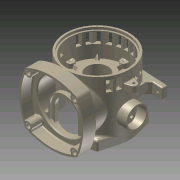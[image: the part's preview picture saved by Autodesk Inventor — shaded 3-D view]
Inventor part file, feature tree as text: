
AUTODESK INVENTOR PART (.ipt)
format: ipt  version: 2011 (Build 150239000, 239)  size: 2,364,928 bytes
history: native  units: in
note: dims shown in document units (in); Inventor stores cm internally (conversion verified against a paired STEP export)
features: extrude x28, sketch x24, plane x15, projected_geometry x10, loft x4, fillet x3, mirror x1, revolve x1, pattern_circular x1, chamfer x1
ambient origin geometry x8: Origin, YZ Plane, XZ Plane, XY Plane, X Axis, Y Axis, Z Axis, Center Point
bodies: Solid1 (feature_tree)
feature tree (88):
  extrude  "Extrusion1"  Depth=2.425in
  extrude  "Extrusion2"  Depth=0.1625in
  plane  "Work Plane3"
  sketch  "Sketch4"  dims[d7=3.375in d8=0.1in]
  plane  "Work Plane4"
  extrude  "Extrusion3"  Depth=0.1in
  sketch  "Sketch6"  dims[d11=0.1in d15=2.6693in]
  extrude  "Extrusion6"  Depth=0.1in
  extrude  "Extrusion7"  Depth=2.6693in
  sketch  "Sketch8"  dims[d19=2.625in d20=0.1in d21=0.0in]
  extrude  "Extrusion8"  Depth=0.575in TaperAngle=0.0deg
  extrude  "Extrusion10"  Depth=0.1in TaperAngle=0.0deg
  plane  "Work Plane5"
  sketch  "Sketch9"  dims[d24=3.15in d25=0.1in]
  extrude  "Extrusion12"  Depth=0.1in
  extrude  "Extrusion13"  Depth=0.1625in
  plane  "Work Plane6"
  extrude  "Extrusion15"  Depth=0.1in TaperAngle=0.0deg
  extrude  "Extrusion16"  Depth=0.5in TaperAngle=0.0deg
  plane  "Work Plane7"
  plane  "Work Plane8"
  plane  "Work Plane9"
  sketch  "Sketch15"  dims[d43=2.725in d44=0.0in d47=2.725in d48=0.0in]
  sketch  "Sketch13"  dims[d35=0.1in d38=0.5in d39=0.0in]
  extrude  "Extrusion19"  Depth=0.1in
  extrude  "Extrusion20"  Depth=2.725in TaperAngle=0.0deg
  plane  "Work Plane11"
  sketch  "Sketch14"  dims[d40=2.725in d41=0.0in d42=0.1in]
  extrude  "Extrusion21"  Depth=1.7in
  plane  "Work Plane12"
  extrude  "Extrusion22"  Depth=0.25in
  mirror  "Mirror3"
  extrude  "Extrusion23"  Depth=2.725in TaperAngle=0.0deg
  plane  "Work Plane15"
  sketch  "Sketch20"  dims[d55=0.0625in d58=2.725in d59=0.0in]
  plane  "Work Plane16"
  plane  "Work Plane17"
  extrude  "Extrusion30"  Depth=0.1in TaperAngle=0.0deg
  extrude  "Extrusion25"  Depth=0.75in
  extrude  "Extrusion26"  Depth=1.185in
  extrude  "Extrusion27"  Depth=0.25in TaperAngle=0.0deg
  extrude  "Extrusion29"  TaperAngle=0.0deg  [1 undecoded]
  extrude  "Extrusion31"  Depth=0.2375in
  extrude  "Extrusion32"  Depth=0.175in
  plane  "Work Plane18"
  extrude  "Extrusion33"  Depth=1.5748in
  plane  "Work Plane19"
  revolve  "Revolution1"  [1 undecoded]
  pattern_circular  "Circular Pattern1"  [2 undecoded]
  extrude  "Extrusion34"  Depth=0.7874in
  extrude  "Extrusion36"  Depth=0.675in
  sketch  "Sketch29"  dims[d83=0.25in d84=0.0in d85=0.2375in]
  plane  "Work Plane20"
  sketch  "Sketch30"  dims[d86=0.55in d87=0.175in]
  loft  "Loft1"
  loft  "Loft2"
  loft  "Loft3"
  loft  "Loft4"
  extrude  "Extrusion37"  Depth=0.4125in
  extrude  "Extrusion38"  Depth=1.0in
  fillet  "Fillet1"  Radius=1.1375in
  fillet  "Fillet3"  Radius=1.25in
  fillet  "Fillet4"  Radius=0.25in
  chamfer  "Chamfer1"  Distance=0.25in
  sketch  "Sketch1"  dims[d0=0.25in d1=2.425in]
  sketch  "Sketch2"  dims[d4=2.425in d5=0.1625in]
  projected_geometry  "Projected Loop1"
  projected_geometry  "Projected Loop2"
  sketch  "Sketch5"  dims[d9=0.1in d10=0.1in]
  sketch  "Sketch7"  dims[d16=2.6693in d17=0.575in d18=0.0in]
  projected_geometry  "Projected Loop3"
  projected_geometry  "Projected Loop4"
  sketch  "Sketch11"  dims[d27=0.25in d29=0.1625in]
  sketch  "Sketch12"  dims[d30=-0.05in d31=0.1in d32=0.0in]
  sketch  "Sketch16"  dims[d49=-0.125in d50=1.7in]
  sketch  "Sketch18"  dims[d51=0.25in d52=0.25in]
  projected_geometry  "Projected Loop6"
  sketch  "Sketch23"  dims[d60=0.175in d61=0.1in d62=0.0in]
  sketch  "Sketch24"  dims[d65=4.0in d66=0.75in]
  projected_geometry  "Projected Loop8"
  sketch  "Sketch25"  dims[d67=0.575in d69=1.185in]
  projected_geometry  "Projected Loop9"
  projected_geometry  "Projected Loop10"
  sketch  "Sketch26"  dims[d71=2.001in d72=0.25in d73=0.0in]
  sketch  "Sketch28"  dims[d81=0.375in d82=0.0in]
  projected_geometry  "Projected Loop12"
  sketch  "Sketch31"  dims[d95=1.5748in d97=0.3625in d98=0.3937in d100=1.0in d102=1.5748in d104=0.3625in d105=0.3937in d107=1.0in d111=0.2375in d112=0.7in d113=0.7874in d115=0.3625in d116=0.3937in d118=1.0in d120=0.675in d121=0.125in d122=0.2375in d123=0.2375in d124=3.05in d127=0.4125in d128=1.0in d129=1.1375in d130=1.25in d131=0.25in d132=0.0in d133=0.25in d134=0.0in d136=-0.5in d139=0.375in d140=0.125in d141=0.375in d142=0.0in d143=1.9175in d147=-0.125in d148=0.635in d149=0.5in d151=0.325in d152=0.375in d153=0.0in d154=0.375in d155=0.0in d156=1.1811in d158=360.0deg d160=0.175in d161=0.275in d167=-1.835in d168=0.1in d169=0.0in d170=1.125in d172=0.25in d173=0.175in d174=0.375in d175=0.175in d177=0.4125in d178=0.0in d179=45.0deg d180=0.175in d181=0.1875in d182=0.0875in d183=0.25in d184=0.0in d185=90.0deg d189=90.0deg d190=0.25in d191=0.175in d192=1.0in d193=0.0in d194=0.075in d195=1.265in d196=0.0in d197=1.265in d198=0.0in d199=1.265in d200=0.0in d201=90.0deg d202=0.175in d203=0.25in d204=1.265in d205=0.0in d206=90.0deg d208=0.175in d209=0.025in d210=90.0deg d211=1.5748in d212=360.0deg d214=0.0625in d216=0.375in d217=1.265in d218=0.0in d221=1.265in d222=0.0in d223=0.0312in d224=0.0312in d225=0.125in d226=0.125in d227=90.0deg d228=2.45in d229=-0.05in d230=0.225in d231=1.5748in d233=360.0deg d235=0.0in d236=90.0deg d237=0.0in d238=90.0deg d239=0.0in d240=90.0deg d241=0.0in d242=90.0deg d243=0.0in d244=90.0deg d245=0.0in d246=90.0deg d247=0.0in d248=90.0deg d249=0.0in d250=90.0deg d251=0.375in d252=0.0in d253=0.125in d254=0.0156in d255=0.125in d256=1.265in d257=0.0in d258=0.025in d259=0.125in d260=45.0deg]
  projected_geometry  "Projected Loop13"
note: 4 required parameter values undecoded (feature->parameter linkage not recoverable at this tier; creation-order binding heuristic only, values carry confidence <= 0.55)